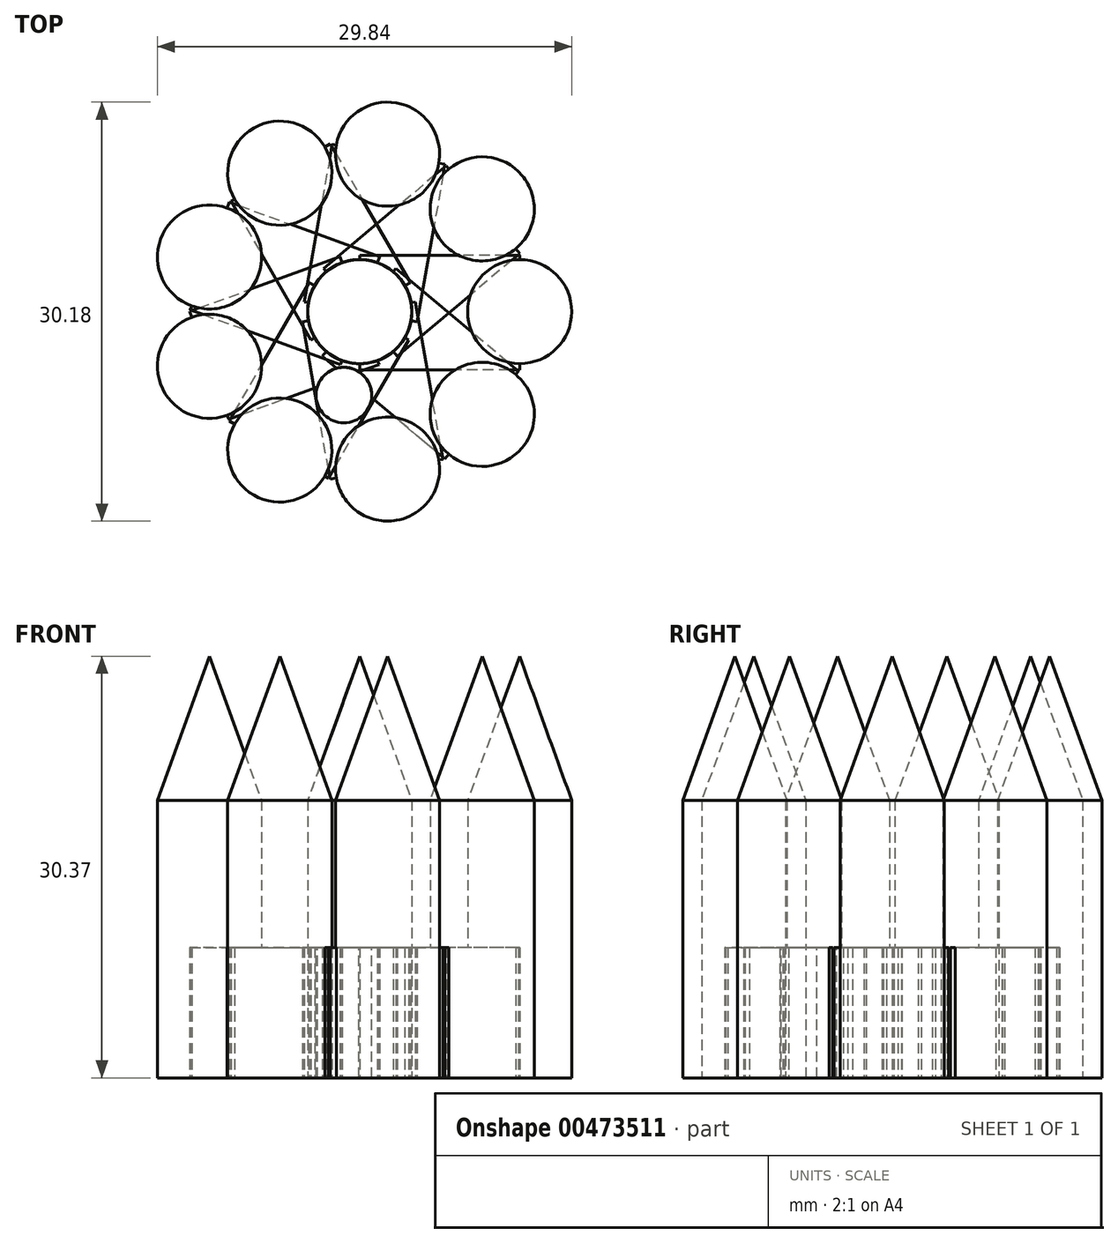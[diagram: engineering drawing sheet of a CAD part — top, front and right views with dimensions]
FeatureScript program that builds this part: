
annotation { "Feature Type Name" : "Feature", "Feature Type Description" : "" }
export const myFeature = defineFeature(function(context is Context, id is Id, definition is map)
    precondition{}
    {
        {
            var Q0;
            Q0=qCreatedBy(makeId("Top.planeOp"),FACE);
            var sketch = newSketch(context, id + "F0", { "sketchPlane" : qUnion([Q0])});
            skCircle(sketch, "E0", {"center": v(0, 0) * mm, "radius": 3.75 * mm});
            skSolve(sketch);
        }
        {
            var Q0;
            Q0=makeQuery(id+"F0.imprint","IMPRINT",FACE,{"disambiguationData":[TD([[makeQuery(id+"F0.imprint","IMPRINT",EDGE,{"derivedFrom":sQuery(id+"F0.wireOp",EDGE,"E0")}),1.0]])]});
            extrude(context, id + "F1", {"entities" : qUnion([Q0]), "depth" : 20 * mm});
        }
        {
            var Q0;
            Q0=qCreatedBy(makeId("Top.planeOp"),FACE);
            var sketch = newSketch(context, id + "F2", { "sketchPlane" : qUnion([Q0])});
            skLineSegment(sketch, "E1.bottom", {"start": v(5.76, 4.05) * mm, "end": v(0, 4.05) * mm});
            skLineSegment(sketch, "E1.top", {"start": v(5.76, -4.2) * mm, "end": v(0, -4.2) * mm});
            skLineSegment(sketch, "E1.left", {"start": v(5.76, 4.05) * mm, "end": v(5.76, -4.2) * mm});
            skLineSegment(sketch, "E1.right", {"start": v(0, 4.05) * mm, "end": v(0, -4.2) * mm});
            skSolve(sketch);
        }
        {
            var Q0;
            Q0=makeQuery(id+"F2.imprint","IMPRINT",FACE,{"disambiguationData":[TD([[makeQuery(id+"F2.imprint","IMPRINT",EDGE,{"derivedFrom":sQuery(id+"F2.wireOp",EDGE,"E1.bottom")}),1.0]])]});
            extrude(context, id + "F3", {"entities" : qUnion([Q0]), "operationType" : NewBodyOperationType.ADD, "depth" : 9.4 * mm});
        }
        {
            var Q0;
            Q0=qCreatedBy(makeId("Front.planeOp"),FACE);
            var sketch = newSketch(context, id + "F4", { "sketchPlane" : qUnion([Q0])});
            skLineSegment(sketch, "E2", {"start": v(0, 20) * mm, "end": v(0, 30.37) * mm});
            skLineSegment(sketch, "E3", {"start": v(0, 20) * mm, "end": v(3.75, 20) * mm});
            skLineSegment(sketch, "E4", {"start": v(3.75, 20) * mm, "end": v(0, 30.37) * mm});
            skSolve(sketch);
        }
        {
            var Q0;
            Q0 = qSketchRegion(id + "F4", true);
            var Q1;
            Q1=sQuery(id+"F4.wireOp",EDGE,"E2");
            revolve(context, id + "F5", {"operationType" : NewBodyOperationType.ADD, "entities" : qUnion([Q0]), "axis" : qUnion([Q1]), "revolveType" : RevolveType.FULL});
        }
        {
            var Q0;
            Q0=makeQuery(id+"F1.opExtrude","SWEPT_BODY",BODY,{"disambiguationData":[OSD([sQuery(id+"F0.wireOp",EDGE,"E0")])]});
            var Q1;
            Q1=makeQuery(id+"F3.opExtrude","SWEPT_FACE",FACE,{"disambiguationData":[OSD([sQuery(id+"F2.wireOp",EDGE,"E1.left")])]});
            mirror(context, id + "F6", {"operationType" : NewBodyOperationType.ADD, "entities" : qUnion([Q0]), "mirrorPlane" : qUnion([Q1])});
        }
        {
            var Q0;
            Q0=qCreatedBy(makeId("Front.planeOp"),FACE);
            var sketch = newSketch(context, id + "F7", { "sketchPlane" : qUnion([Q0])});
            skLineSegment(sketch, "E5", {"start": v(0, 0) * mm, "end": v(0, 19.98) * mm});
            skSolve(sketch);
        }
        {
            var Q0;
            Q0=makeQuery(id+"F1.opExtrude","SWEPT_BODY",BODY,{"disambiguationData":[OSD([sQuery(id+"F0.wireOp",EDGE,"E0")])]});
            var Q1;
            Q1=sQuery(id+"F7.wireOp",EDGE,"E5");
            circularPattern(context, id + "F8", {"entities" : qUnion([Q0]), "axis" : qUnion([Q1]), "angle" : 360 * degree, "instanceCount" : 9, "equalSpace" : true});
        }
        {
            var Q0;
            {var subQ0=makeQuery(id+"F3.opExtrude","CAP_FACE",FACE,{"disambiguationData":[OSD([sQuery(id+"F2.wireOp",EDGE,"E1.bottom"),sQuery(id+"F2.wireOp",EDGE,"E1.top"),sQuery(id+"F2.wireOp",EDGE,"E1.left"),sQuery(id+"F2.wireOp",EDGE,"E1.right")])],"isStart":false});Q0=makeQuery(id+"F8.opPattern","COPY",FACE,{"derivedFrom":makeQuery(id+"F6.boolean.opBoolean","MERGE",FACE,{"derivedFrom":[subQ0,makeQuery(id+"F6.opPattern","COPY",FACE,{"derivedFrom":subQ0,"instanceName":"1"})]}),"instanceName":"6"});}
            var sketch = newSketch(context, id + "F9", { "sketchPlane" : qUnion([Q0])});
            skLineSegment(sketch, "E6", {"start": v(0.15, 1.27) * mm, "end": v(-5.6, -8.68) * mm});
            skLineSegment(sketch, "E7", {"start": v(-5.6, -8.68) * mm, "end": v(2.14, -9.88) * mm});
            skLineSegment(sketch, "E8", {"start": v(2.14, -9.88) * mm, "end": v(0.15, 1.27) * mm});
            skLineSegment(sketch, "E9", {"start": v(0.15, 1.27) * mm, "end": v(-1.73, -9.28) * mm});
            skLineSegment(sketch, "E10", {"start": v(-5.6, -8.68) * mm, "end": v(1.15, -4.3) * mm});
            skLineSegment(sketch, "E11", {"start": v(2.14, -9.88) * mm, "end": v(-2.72, -3.7) * mm});
            skCircle(sketch, "E12", {"center": v(-1.14, -6.01) * mm, "radius": 2 * mm});
            skSolve(sketch);
        }
        {
            var Q0;
            {var subQ0=sQuery(id+"F9.wireOp",EDGE,"E12");var subQ1=sQuery(id+"F9.wireOp",EDGE,"E10");var subQ2=makeQuery(id+"F9.imprint","INTERSECT",VERTEX,{"disambiguationData":[OD(0.0)],"derivedFrom":[subQ1,subQ0]});Q0=makeQuery(id+"F9.imprint","IMPRINT",FACE,{"disambiguationData":[TD([[makeQuery(id+"F9.imprint","IMPRINT",EDGE,{"disambiguationData":[TD([[subQ2,1.0]])],"derivedFrom":subQ0}),1.0]])]});}
            var Q1;
            {var subQ0=sQuery(id+"F9.wireOp",EDGE,"E12");var subQ1=sQuery(id+"F9.wireOp",EDGE,"E9");var subQ2=makeQuery(id+"F9.imprint","INTERSECT",VERTEX,{"disambiguationData":[OD(1.0)],"derivedFrom":[subQ1,subQ0]});Q1=makeQuery(id+"F9.imprint","IMPRINT",FACE,{"disambiguationData":[TD([[makeQuery(id+"F9.imprint","IMPRINT",EDGE,{"disambiguationData":[TD([[subQ2,1.0]])],"derivedFrom":subQ0}),1.0]])]});}
            var Q2;
            {var subQ0=sQuery(id+"F9.wireOp",EDGE,"E12");var subQ1=sQuery(id+"F9.wireOp",EDGE,"E9");var subQ2=makeQuery(id+"F9.imprint","INTERSECT",VERTEX,{"disambiguationData":[OD(1.0)],"derivedFrom":[subQ1,subQ0]});Q2=makeQuery(id+"F9.imprint","IMPRINT",FACE,{"disambiguationData":[TD([[makeQuery(id+"F9.imprint","IMPRINT",EDGE,{"disambiguationData":[TD([[subQ2,-1.0]])],"derivedFrom":subQ0}),1.0]])]});}
            var Q3;
            {var subQ0=sQuery(id+"F9.wireOp",EDGE,"E12");var subQ1=sQuery(id+"F9.wireOp",EDGE,"E10");var subQ2=makeQuery(id+"F9.imprint","INTERSECT",VERTEX,{"disambiguationData":[OD(1.0)],"derivedFrom":[subQ1,subQ0]});Q3=makeQuery(id+"F9.imprint","IMPRINT",FACE,{"disambiguationData":[TD([[makeQuery(id+"F9.imprint","IMPRINT",EDGE,{"disambiguationData":[TD([[subQ2,1.0]])],"derivedFrom":subQ0}),1.0]])]});}
            var Q4;
            {var subQ0=sQuery(id+"F9.wireOp",EDGE,"E12");var subQ1=sQuery(id+"F9.wireOp",EDGE,"E9");var subQ2=makeQuery(id+"F9.imprint","INTERSECT",VERTEX,{"disambiguationData":[OD(0.0)],"derivedFrom":[subQ1,subQ0]});Q4=makeQuery(id+"F9.imprint","IMPRINT",FACE,{"disambiguationData":[TD([[makeQuery(id+"F9.imprint","IMPRINT",EDGE,{"disambiguationData":[TD([[subQ2,1.0]])],"derivedFrom":subQ0}),1.0]])]});}
            var Q5;
            {var subQ0=sQuery(id+"F9.wireOp",EDGE,"E12");var subQ1=sQuery(id+"F9.wireOp",EDGE,"E9");var subQ2=makeQuery(id+"F9.imprint","INTERSECT",VERTEX,{"disambiguationData":[OD(0.0)],"derivedFrom":[subQ1,subQ0]});Q5=makeQuery(id+"F9.imprint","IMPRINT",FACE,{"disambiguationData":[TD([[makeQuery(id+"F9.imprint","IMPRINT",EDGE,{"disambiguationData":[TD([[subQ2,-1.0]])],"derivedFrom":subQ0}),1.0]])]});}
            var Q6;
            Q6=sQuery(id+"F9.wireOp",EDGE,"E12");
            extrude(context, id + "F10", {"entities" : qUnion([Q0, Q1, Q2, Q3, Q4, Q5]), "operationType" : NewBodyOperationType.REMOVE, "surfaceEntities" : qUnion([Q6]), "oppositeDirection" : true, "depth" : 25 * mm});
        }
    });
